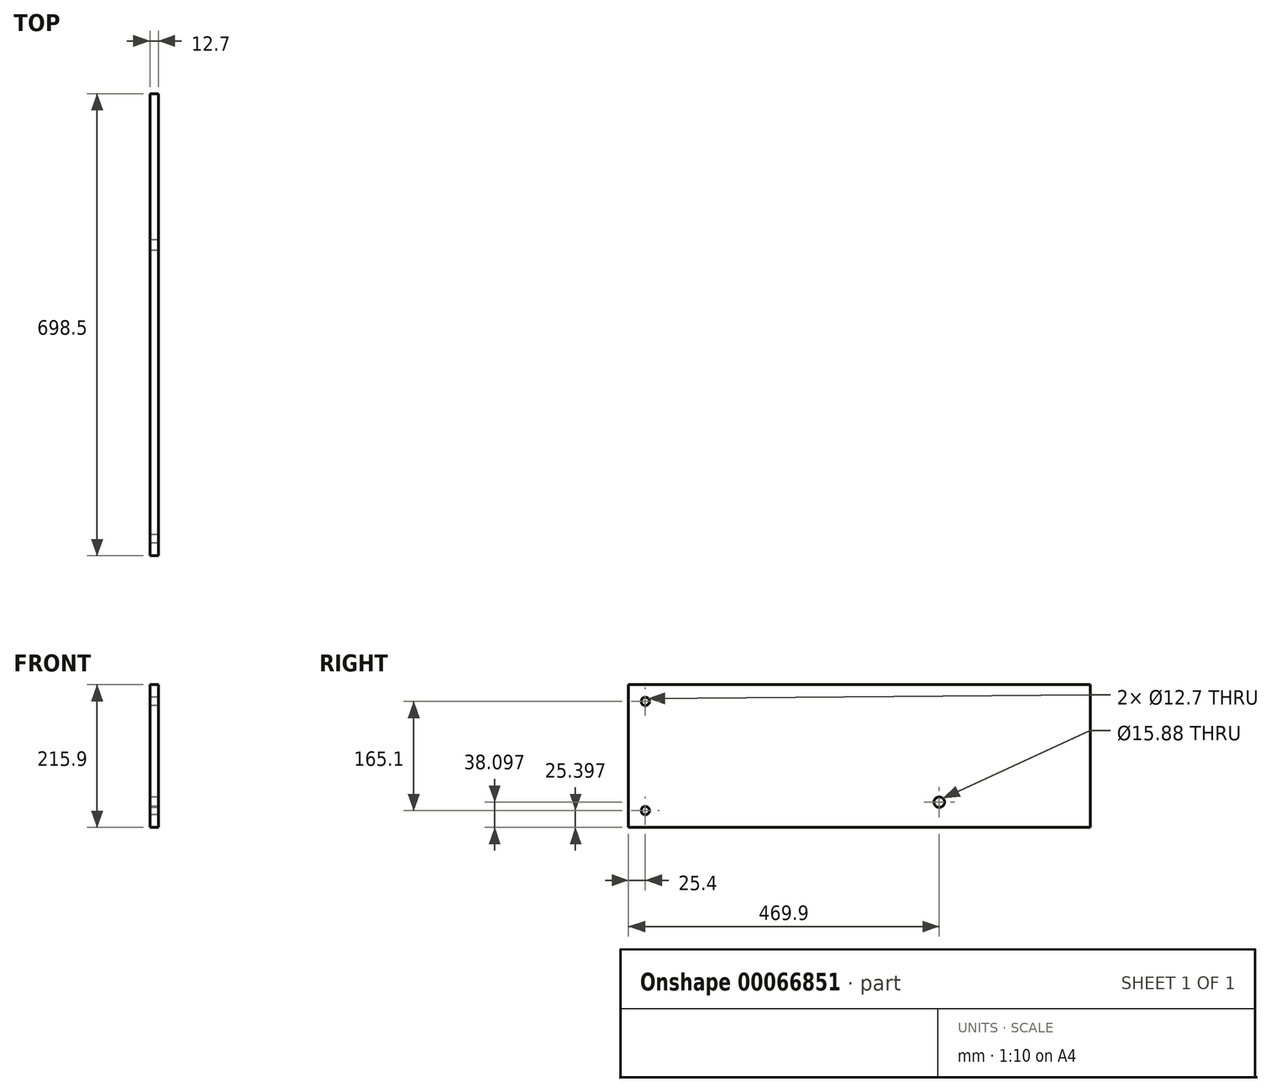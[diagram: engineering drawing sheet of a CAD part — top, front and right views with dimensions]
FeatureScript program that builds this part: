
annotation { "Feature Type Name" : "Feature", "Feature Type Description" : "" }
export const myFeature = defineFeature(function(context is Context, id is Id, definition is map)
    precondition{}
    {
        {
            var Q0;
            Q0=qCreatedBy(makeId("Right.planeOp"),FACE);
            var sketch = newSketch(context, id + "F0", { "sketchPlane" : qUnion([Q0])});
            skLineSegment(sketch, "E0.bottom", {"start": v(-469.9, 166.42) * mm, "end": v(228.6, 166.42) * mm});
            skLineSegment(sketch, "E0.top", {"start": v(-469.9, -49.48) * mm, "end": v(228.6, -49.48) * mm});
            skLineSegment(sketch, "E0.left", {"start": v(-469.9, 166.42) * mm, "end": v(-469.9, -49.48) * mm});
            skLineSegment(sketch, "E0.right", {"start": v(228.6, 166.42) * mm, "end": v(228.6, -49.48) * mm});
            skCircle(sketch, "E1", {"center": v(0, -11.38) * mm, "radius": 7.94 * mm});
            skCircle(sketch, "E2", {"center": v(-444.5, -24.08) * mm, "radius": 6.35 * mm});
            skCircle(sketch, "E3", {"center": v(-444.5, 141.02) * mm, "radius": 6.35 * mm});
            skSolve(sketch);
        }
        {
            var Q0;
            Q0=makeQuery(id+"F0.imprint","IMPRINT",FACE,{"disambiguationData":[TD([[makeQuery(id+"F0.imprint","IMPRINT",EDGE,{"derivedFrom":sQuery(id+"F0.wireOp",EDGE,"E0.bottom")}),-1.0]])]});
            extrude(context, id + "F1", {"entities" : qUnion([Q0]), "depth" : 12.7 * mm});
        }
    });
